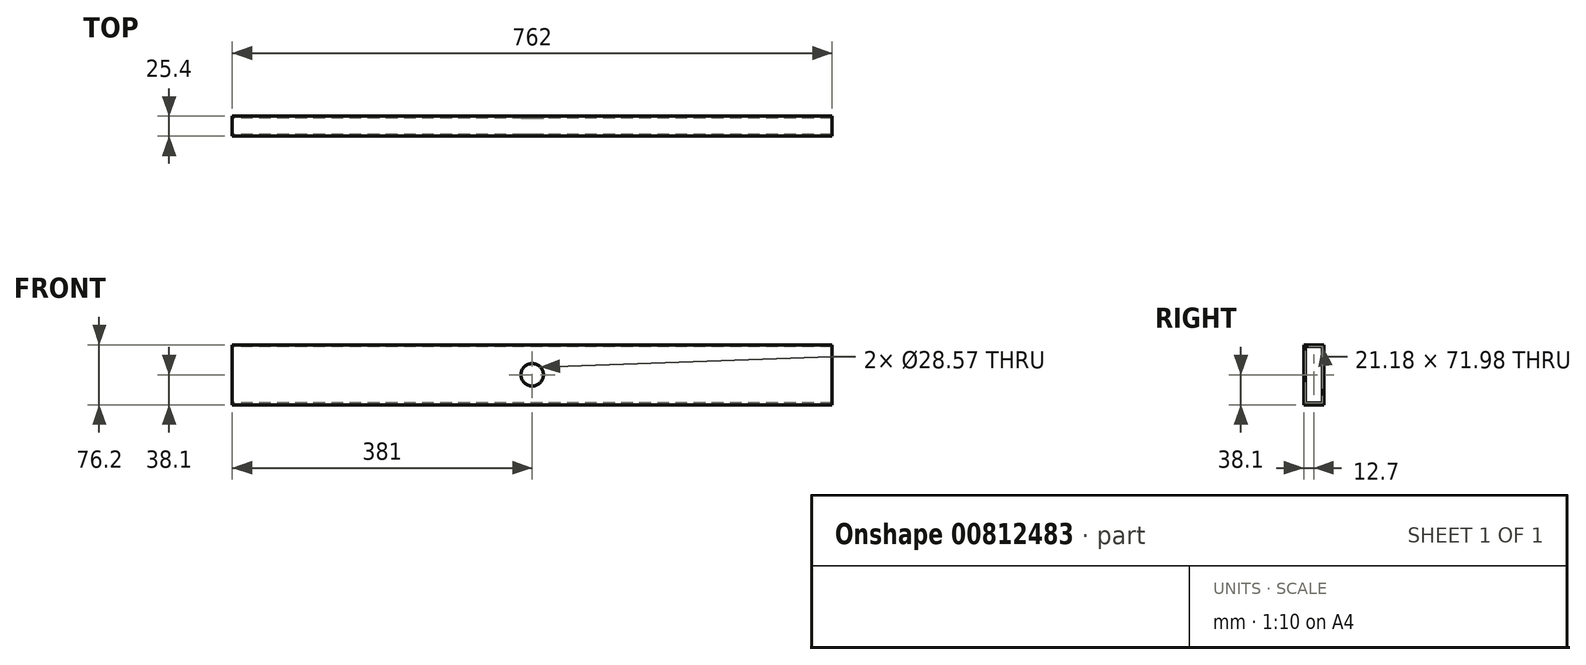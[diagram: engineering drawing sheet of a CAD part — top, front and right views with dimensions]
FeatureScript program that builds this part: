
annotation { "Feature Type Name" : "Feature", "Feature Type Description" : "" }
export const myFeature = defineFeature(function(context is Context, id is Id, definition is map)
    precondition{}
    {
        {
            var Q0;
            Q0=qCreatedBy(makeId("Right.planeOp"),FACE);
            var sketch = newSketch(context, id + "F0", { "sketchPlane" : qUnion([Q0])});
            skLineSegment(sketch, "E0.bottom", {"start": v(12.7, 38.1) * mm, "end": v(-12.7, 38.1) * mm});
            skLineSegment(sketch, "E0.top", {"start": v(12.7, -38.1) * mm, "end": v(-12.7, -38.1) * mm});
            skLineSegment(sketch, "E0.left", {"start": v(12.7, 38.1) * mm, "end": v(12.7, -38.1) * mm});
            skLineSegment(sketch, "E0.right", {"start": v(-12.7, 38.1) * mm, "end": v(-12.7, -38.1) * mm});
            skPoint(sketch, "E0.middle", {"position": v(0, 0) * mm});
            skLineSegment(sketch, "E1.0", {"start": v(10.6, 36) * mm, "end": v(-10.6, 36) * mm});
            skLineSegment(sketch, "E1.1", {"start": v(10.6, 36) * mm, "end": v(10.6, -36) * mm});
            skLineSegment(sketch, "E1.2", {"start": v(10.6, -36) * mm, "end": v(-10.6, -36) * mm});
            skLineSegment(sketch, "E1.3", {"start": v(-10.6, 36) * mm, "end": v(-10.6, -36) * mm});
            skSolve(sketch);
        }
        {
            var Q0;
            Q0=makeQuery(id+"F0.imprint","IMPRINT",FACE,{"disambiguationData":[TD([[makeQuery(id+"F0.imprint","IMPRINT",EDGE,{"derivedFrom":sQuery(id+"F0.wireOp",EDGE,"E0.bottom")}),1.0]])]});
            extrude(context, id + "F1", {"entities" : qUnion([Q0]), "endBound" : BoundingType.SYMMETRIC, "depth" : 762 * mm, "offsetDistance" : 25.4 * mm});
        }
        {
            var Q0;
            Q0=makeQuery(id+"F1.opExtrude","SWEPT_FACE",FACE,{"disambiguationData":[OSD([sQuery(id+"F0.wireOp",EDGE,"E0.right")])]});
            var sketch = newSketch(context, id + "F2", { "sketchPlane" : qUnion([Q0])});
            skCircle(sketch, "E2", {"center": v(0, 0) * mm, "radius": 14.29 * mm});
            skSolve(sketch);
        }
        {
            var Q0;
            Q0 = qSketchRegion(id + "F2", true);
            extrude(context, id + "F3", {"entities" : qUnion([Q0]), "operationType" : NewBodyOperationType.REMOVE, "endBound" : BoundingType.THROUGH_ALL, "oppositeDirection" : true, "depth" : 25.4 * mm, "offsetDistance" : 25.4 * mm});
        }
    });
